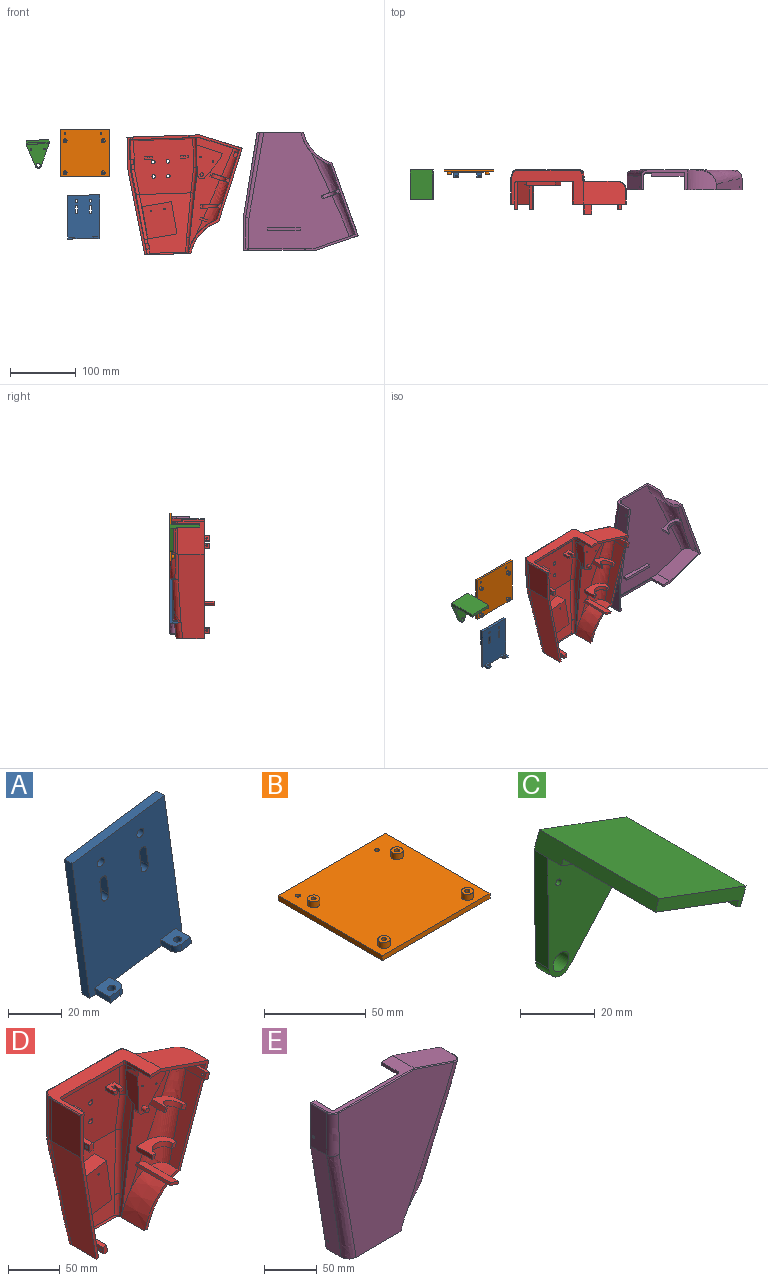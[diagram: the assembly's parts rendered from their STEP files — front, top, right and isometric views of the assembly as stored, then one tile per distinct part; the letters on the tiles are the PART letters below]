
ASSEMBLY  parts=5 mates=5
PART A: 28 faces, bbox 57.8x12x73 mm
  f0: plane 8x2.97mm, normal (-0.99,0,-0.14), area 24mm2, adj f1,f3,f4,f8
  f1: plane 8x7.92mm, normal (-0.14,0,0.99), area 55mm2, adj f0,f2,f4,f6,f7,f8
  f2: plane 5x2.97mm, normal (0.99,0,0.14), area 15mm2, adj f1,f3,f7,f8
  f3: plane 48.52x12mm, normal (0.14,0,-0.99), area 306mm2, adj f0,f2,f4,f5,f6,f7,f8,f9
  f4: plane 5.37x3.67mm, normal (0,-1,0), area 15mm2, adj f0,f1,f3,f7
  f5: plane 72.97x57.82mm, normal (0,1,0), area 3171mm2, adj f3,f15,f16,f17,f18,f19,f20,f21
  f6: cylinder r=1.5mm len=3.39mm, axis (0.14,0,-0.99), area 28.3mm2, adj f1,f3
  f7: cylinder r=3mm len=3.39mm, axis (-0.14,0,0.99), area 14.1mm2, adj f1,f2,f3,f4
  f8: plane 72.97x57.82mm, normal (0,-1,0), area 3123mm2, adj f0,f1,f2,f3,f9,f10,f11,f15
  f9: plane 5x2.97mm, normal (-0.99,0,-0.14), area 15mm2, adj f3,f8,f10,f14
  f10: plane 8x7.92mm, normal (-0.14,0,0.99), area 55mm2, adj f8,f9,f11,f12,f13,f14
  f11: plane 8x2.97mm, normal (0.99,0,0.14), area 24mm2, adj f3,f8,f10,f12
  f12: plane 5.37x3.67mm, normal (0,-1,0), area 15mm2, adj f3,f10,f11,f14
  f13: cylinder r=1.5mm len=3.39mm, axis (0.14,0,-0.99), area 28.3mm2, adj f3,f10
  f14: cylinder r=3mm len=3.39mm, axis (0.14,0,-0.99), area 14.1mm2, adj f3,f9,f10,f12
  f15: plane 48.52x6.82mm, normal (-0.14,0,0.99), area 196mm2, adj f5,f8,f16,f17
  f16: plane 66.15x9.3mm, normal (0.99,0,0.14), area 267.2mm2, adj f3,f5,f8,f15
  f17: plane 66.15x9.3mm, normal (-0.99,0,-0.14), area 267.2mm2, adj f3,f5,f8,f15
  f18: cylinder r=1.85mm len=4mm, axis (0,1,0), area 46.5mm2, adj f5,f8
  f19: cylinder r=1.85mm len=4mm, axis (0,1,0), area 46.5mm2, adj f5,f8
  f20: plane 7.92x4mm, normal (-0.99,0,-0.14), area 32mm2, adj f5,f8,f21,f23
  f21: cylinder r=1.85mm len=4mm, axis (0,-1,0), area 23.2mm2, adj f5,f8,f20,f22
  f22: plane 7.92x4mm, normal (0.99,0,0.14), area 32mm2, adj f5,f8,f21,f23
  f23: cylinder r=1.85mm len=4mm, axis (0,-1,0), area 23.2mm2, adj f5,f8,f20,f22
  f24: plane 7.92x4mm, normal (-0.99,0,-0.14), area 32mm2, adj f5,f8,f25,f27
  f25: cylinder r=1.85mm len=4mm, axis (0,-1,0), area 23.2mm2, adj f5,f8,f24,f26
  f26: plane 7.92x4mm, normal (0.99,0,0.14), area 32mm2, adj f5,f8,f25,f27
  f27: cylinder r=1.85mm len=4mm, axis (0,-1,0), area 23.2mm2, adj f5,f8,f24,f26
PART B: 20 faces, bbox 75x72.5x6.5 mm
  f0: plane 75x3mm, normal (0,-1,0), area 225mm2, adj f1,f3,f4,f5
  f1: plane 75x72.5mm, normal (0,0,-1), area 5408mm2, adj f0,f2,f3,f4,f14,f15,f16,f17
  f2: plane 75x3mm, normal (0,1,0), area 225mm2, adj f1,f3,f4,f5
  f3: plane 72.5x3mm, normal (1,0,0), area 217.5mm2, adj f0,f1,f2,f5
  f4: plane 72.5x3mm, normal (-1,0,0), area 217.5mm2, adj f0,f1,f2,f5
  f5: plane 75x72.5mm, normal (0,0,1), area 5314.6mm2, adj f0,f2,f3,f4,f6,f8,f10,f12
  f6: cylinder r=3mm len=6mm, axis (0,0,-1), area 66mm2, adj f5,f7
  f7: plane 6x6mm, normal (0,0,1), area 23.4mm2, adj f6,f14
  f8: cylinder r=3mm len=6mm, axis (0,0,-1), area 66mm2, adj f5,f9
  f9: plane 6x6mm, normal (0,0,1), area 23.4mm2, adj f8,f15
  f10: cylinder r=3mm len=6mm, axis (0,0,-1), area 66mm2, adj f5,f11
  f11: plane 6x6mm, normal (0,0,1), area 23.4mm2, adj f10,f17
  f12: cylinder r=3mm len=6mm, axis (0,0,-1), area 66mm2, adj f5,f13
  f13: plane 6x6mm, normal (0,0,1), area 23.4mm2, adj f12,f16
  f14: cylinder r=1.25mm len=6.5mm, axis (0,0,-1), area 51.1mm2, adj f1,f7
  f15: cylinder r=1.25mm len=6.5mm, axis (0,0,-1), area 51.1mm2, adj f1,f9
  f16: cylinder r=1.25mm len=6.5mm, axis (0,0,-1), area 51.1mm2, adj f1,f13
  f17: cylinder r=1.25mm len=6.5mm, axis (0,0,-1), area 51.1mm2, adj f1,f11
  f18: cylinder r=1.25mm len=3mm, axis (0,0,-1), area 23.6mm2, adj f1,f5
  f19: cylinder r=1.25mm len=3mm, axis (0,0,-1), area 23.6mm2, adj f1,f5
PART C: 16 faces, bbox 34.9x45.1x46.6 mm
  f0: plane 34.75x31.39mm, normal (-0.35,0,-0.94), area 1164.4mm2, adj f3,f4,f5,f6
  f1: plane 45.1x5.62mm, normal (0.94,0,-0.35), area 270.6mm2, adj f2,f4,f7,f8,f12
  f2: plane 45.1x32.79mm, normal (0.35,0,0.94), area 1578.5mm2, adj f1,f3,f4,f12
  f3: plane 45.1x5.62mm, normal (-0.94,0,0.35), area 201.1mm2, adj f0,f2,f4,f6,f7,f10,f12
  f4: plane 34.19x17.86mm, normal (0,-1,0), area 143mm2, adj f0,f1,f2,f3,f5,f7
  f5: plane 34.75x1.87mm, normal (-0.94,0,0.35), area 69.5mm2, adj f0,f4,f6,f7
  f6: plane 32.09x13.59mm, normal (0,-1,0), area 67mm2, adj f0,f3,f5,f7
  f7: plane 40x32.79mm, normal (-0.35,0,-0.94), area 235.6mm2, adj f1,f3,f4,f5,f6,f13
  f8: plane 27.21x24.34mm, normal (0.75,0,-0.67), area 186.2mm2, adj f1,f9,f12,f13
  f9: cylinder r=4.53mm len=7.9mm, axis (0,-1,0), area 55.3mm2, adj f8,f10,f12,f13
  f10: plane 36.5x5.1mm, normal (-1,0,-0.02), area 186.2mm2, adj f3,f9,f12,f13
  f11: cylinder r=3mm len=6mm, axis (0,-1,0), area 96.1mm2, adj f12,f13
  f12: plane 46.58x34.89mm, normal (0,1,0), area 931.4mm2, adj f1,f2,f3,f8,f9,f10,f11,f14
  f13: plane 40.96x32.79mm, normal (0,-1,0), area 721.4mm2, adj f7,f8,f9,f10,f11,f14,f15
  f14: cylinder r=1mm len=5.1mm, axis (0,-1,0), area 32mm2, adj f12,f13
  f15: cylinder r=1mm len=5.1mm, axis (0,-1,0), area 32mm2, adj f12,f13
PART D: 191 faces, bbox 178.3x70.2x193.3 mm
  f0: plane 89.97x78.42mm, normal (0,-0.99,0.11), area 3717.7mm2, adj f6,f22,f24,f26,f96,f97,f99,f100
  f1: bspline ~107.95x56.06mm, area 927.7mm2, adj f2,f93,f162,f176
  f2: plane 175.95x74.2mm, normal (0,-1,0), area 3207.5mm2, adj f1,f3,f4,f17,f21,f30,f76,f77
  f3: bspline ~141.8x71.41mm, area 740.7mm2, adj f2,f21,f93,f168,f169,f171,f174,f175
  f4: bspline ~118.22x59.84mm, area 747.7mm2, adj f2,f93,f94,f105,f107,f108,f109,f161
  f5: plane 14.86x7.7mm, normal (-0.99,-0.14,0), area 104.2mm2, adj f77,f82,f83,f95,f147
  f6: plane 90.13x82.27mm, normal (0,-1,0), area 6994.7mm2, adj f0,f83,f95,f96,f98,f99,f101,f102
  f7: plane 180x24.73mm, normal (0,-1,0), area 644.5mm2, adj f10,f20,f27,f32,f75,f91,f92,f124
  f8: plane 180x86.88mm, normal (0,-1,0), area 927.3mm2, adj f11,f21,f27,f30,f33,f34,f62,f93
  f9: plane 178.26x71.96mm, normal (0,1,0), area 4250mm2, adj f11,f14,f35,f42,f64,f125
  f10: plane 130x39.85mm, normal (-0.99,0,-0.16), area 4906.6mm2, adj f7,f16,f32,f45,f48,f125
  f11: cylinder r=64.67mm len=47mm, axis (0,-1,0), area 2206.9mm2, adj f8,f9,f33,f35,f125
  f12: plane 130x18.82mm, normal (0.99,0,-0.14), area 666.7mm2, adj f14,f15,f36,f44,f125
  f13: bspline ~98.25x68.46mm, area 5292.6mm2, adj f15,f16,f50,f53,f54,f58,f125
  f14: bspline ~148.6x23.11mm, area 156.7mm2, adj f9,f12,f42,f125
  f15: bspline ~46x11.51mm, area 150.9mm2, adj f12,f13,f51,f52,f125
  f16: bspline ~41.39x16.37mm, area 394mm2, adj f10,f13,f54,f125
  f17: plane 124.92x18.08mm, normal (-0.99,0,0.14), area 441.8mm2, adj f2,f22,f79,f125,f152
  f18: plane 130.24x21.22mm, normal (0.99,0,0.16), area 659.8mm2, adj f19,f26,f86,f87,f125
  f19: plane 175.58x21.36mm, normal (0,1,0), area 21.9mm2, adj f18,f20,f87,f88,f89,f92,f125
  f20: plane 130.33x30mm, normal (0.99,-0.02,0.16), area 3961.3mm2, adj f7,f19,f92,f125
  f21: cone r=68.17mm half-angle=1deg, axis (0,1,0), area 2093.4mm2, adj f2,f3,f8,f93,f125
  f22: bspline ~32.68x7.93mm, area 132.2mm2, adj f0,f17,f23,f97,f125
  f23: bspline ~3.21x3.08mm, area 1mm2, adj f22,f24,f125
  f24: cylinder r=5mm len=58.35mm, axis (1,0,0), area 133.2mm2, adj f0,f23,f25,f125
  f25: bspline ~3.17x3.08mm, area 1mm2, adj f24,f26,f125
  f26: bspline ~32.83x8.52mm, area 91.6mm2, adj f0,f18,f25,f100,f115,f117,f119,f125
  f27: plane 109x51mm, normal (0,0,1), area 2422.4mm2, adj f7,f8,f34,f66,f67,f68,f69,f70
  f28: plane 10.58x0.12mm, normal (0,1,0), area 1.3mm2, adj f29,f30,f76,f120
  f29: plane 100.2x5mm, normal (0,0,-1), area 78.9mm2, adj f28,f76,f78,f83,f89,f120,f121,f122
  f30: plane 31.53x14.45mm, normal (0,-0.02,-1), area 436.7mm2, adj f2,f8,f28,f76,f94,f120
  f31: plane 44.7x7.7mm, normal (0.99,-0.14,0), area 302.5mm2, adj f83,f84,f85,f86,f88,f98,f110,f112
  f32: plane 49.02x39.9mm, normal (-1,0,0), area 1954.2mm2, adj f7,f10,f48,f49,f75
  f33: plane 110.7x40.16mm, normal (0.94,0,-0.34), area 2131mm2, adj f8,f11,f35,f62
  f34: plane 64.09x35.05mm, normal (0.33,0,0.95), area 2273mm2, adj f8,f27,f62,f63,f64,f65,f66
  f35: bspline ~166.97x81.55mm, area 3387.4mm2, adj f9,f11,f33,f63
  f36: plane 49.01x5.25mm, normal (1,0,0), area 243.8mm2, adj f12,f42,f43,f44,f67
  f37: plane 96.53x95.72mm, normal (0,1,0), area 8197mm2, adj f55,f56,f58,f59,f60,f61,f71,f101
  f38: plane 48.85x5.69mm, normal (0.98,0.2,0), area 275.2mm2, adj f39,f43,f44,f55,f69
  f39: bspline ~140x24.17mm, area 1321.9mm2, adj f38,f44,f50,f51,f55,f56
  f40: bspline ~140x25mm, area 693.8mm2, adj f41,f45,f46,f48,f53,f60,f61
  f41: plane 48x4.9mm, normal (-0.93,0.37,0), area 246.5mm2, adj f40,f48,f49,f61,f73
  f42: bspline ~55.11x2mm, area 132.4mm2, adj f9,f14,f36,f65,f66
  f43: cylinder r=3mm len=48.99mm, axis (0,0,1), area 29mm2, adj f36,f38,f44,f68
  f44: bspline ~108.61x17.07mm, area 135.4mm2, adj f12,f36,f38,f39,f43,f51
  f45: bspline ~76.58x20.42mm, area 787.6mm2, adj f10,f40,f46,f47,f54
  f46: bspline ~5.02x4.67mm, area 3.1mm2, adj f40,f45,f47
  f47: bspline ~5.56x2.24mm, area 2.8mm2, adj f45,f46,f48
  f48: bspline ~41.83x8.47mm, area 180.9mm2, adj f10,f32,f40,f41,f47,f49
  f49: cylinder r=11mm len=48.97mm, axis (0,0,1), area 202.9mm2, adj f32,f41,f48,f74
  f50: bspline ~83.47x9.1mm, area 70.1mm2, adj f13,f39,f52,f57
  f51: bspline ~15.55x5.27mm, area 29.2mm2, adj f15,f39,f44,f52
  f52: bspline ~2.96x1.03mm, area 0.1mm2, adj f15,f50,f51
  f53: bspline ~52.77x5.79mm, area 61.8mm2, adj f13,f40,f54,f59
  f54: bspline ~20.38x12.71mm, area 173mm2, adj f13,f16,f45,f53
  f55: cylinder r=5mm len=46.01mm, axis (0,0,-1), area 314.9mm2, adj f37,f38,f39,f56,f70
  f56: bspline ~42.17x23.6mm, area 184.1mm2, adj f37,f39,f55,f57
  f57: sphere r=5mm, area 0mm2, adj f50,f56,f58
  f58: bspline ~61.72x10.88mm, area 37.4mm2, adj f13,f37,f57,f59
  f59: bspline ~0.51x0.4mm, area 0mm2, adj f37,f53,f58,f60
  f60: bspline ~42.52x23.03mm, area 161.7mm2, adj f37,f40,f59,f61
  f61: cylinder r=5mm len=45.57mm, axis (0,0,-1), area 270.4mm2, adj f37,f40,f41,f60,f72
  f62: cylinder r=1mm len=22mm, axis (0,-1,0), area 34.8mm2, adj f8,f33,f34,f63
  f63: bspline ~17x16.41mm, area 31.3mm2, adj f34,f35,f62,f64
  f64: cylinder r=1mm len=50.72mm, axis (0.95,0,-0.33), area 83.7mm2, adj f9,f34,f63,f65
  f65: bspline ~2.49x1.82mm, area 3mm2, adj f34,f42,f64,f66
  f66: bspline ~2.96x1.75mm, area 2.9mm2, adj f27,f34,f42,f65,f67
  f67: cylinder r=1mm len=4.71mm, axis (0,1,0), area 7.4mm2, adj f27,f36,f66,f68
  f68: torus R=2mm, axis (0,0,1), area 0.8mm2, adj f27,f43,f67,f69
  f69: cylinder r=1mm len=5.89mm, axis (-0.2,0.98,0), area 9.1mm2, adj f27,f38,f68,f70
  f70: torus R=4mm, axis (0,0,1), area 10mm2, adj f27,f55,f69,f71
  f71: cylinder r=1mm len=96.52mm, axis (1,0,0), area 151.6mm2, adj f27,f37,f70,f72
  f72: torus R=4mm, axis (0,0,1), area 8.7mm2, adj f27,f61,f71,f73
  f73: cylinder r=1mm len=5.26mm, axis (-0.37,-0.93,0), area 8.3mm2, adj f27,f41,f72,f74
  f74: torus R=10mm, axis (0,0,1), area 6.4mm2, adj f27,f49,f73,f75
  f75: cylinder r=1mm len=39.88mm, axis (0,-1,0), area 62.6mm2, adj f7,f27,f32,f74
  f76: cylinder r=1mm len=5mm, axis (0,-1,0), area 6.3mm2, adj f2,f28,f29,f30,f77,f82
  f77: plane 11.96x3.5mm, normal (-1,0,0), area 41.9mm2, adj f2,f5,f76,f147
  f78: plane 1.58x0.12mm, normal (0,1,0), area 0.2mm2, adj f29,f89,f91,f124
  f79: plane 106.37x14.61mm, normal (-0.98,-0.14,0.14), area 552.3mm2, adj f17,f80,f81,f96,f97,f152
  f80: cone r=1mm half-angle=8deg, axis (0,-1,0), area 0mm2, adj f79,f81,f152
  f81: plane 14.67x1.59mm, normal (-0.99,-0.14,0), area 11.8mm2, adj f79,f80,f95,f152
  f82: cone r=1mm half-angle=8deg, axis (0,-1,0), area 5.6mm2, adj f5,f76,f83
  f83: plane 100.46x12.26mm, normal (0,-0.14,-0.99), area 1203.1mm2, adj f5,f6,f29,f31,f82,f84,f95,f98
  f84: cone r=1mm half-angle=8deg, axis (0,-1,0), area 5.6mm2, adj f31,f83,f89
  f85: cone r=1mm half-angle=8deg, axis (0,-1,0), area 0.6mm2, adj f31,f86,f87
  f86: plane 106.5x17.33mm, normal (0.98,-0.14,0.16), area 571.3mm2, adj f18,f31,f85,f99,f100
  f87: cylinder r=1mm len=5mm, axis (0,-1,0), area 0.8mm2, adj f18,f19,f85,f88
  f88: plane 44.7x5mm, normal (1,0,0), area 223.5mm2, adj f19,f31,f87,f89
  f89: cylinder r=1mm len=5mm, axis (0,-1,0), area 7.1mm2, adj f19,f29,f78,f84,f88,f90,f91,f92
  f90: plane 0.32x0.32mm, normal (0,-1,0), area 0mm2, adj f89,f91,f92
  f91: plane 31.53x2.53mm, normal (0,-0.02,-1), area 67.7mm2, adj f7,f78,f89,f90,f92,f124
  f92: plane 46.25x31.53mm, normal (1,-0.02,0), area 1378.8mm2, adj f7,f19,f20,f89,f90,f91
  f93: plane 105.64x37.84mm, normal (-0.94,-0.02,0.34), area 1878.9mm2, adj f1,f3,f4,f8,f21,f94,f160,f161
  f94: plane 61.48x31.79mm, normal (-0.33,-0.02,-0.95), area 2009.2mm2, adj f2,f4,f8,f30,f93
  f95: cylinder r=5mm len=44.66mm, axis (0,0,-1), area 307.9mm2, adj f5,f6,f81,f83,f96,f147,f152
  f96: cylinder r=5mm len=39.63mm, axis (-0.14,0,-0.99), area 279.6mm2, adj f0,f6,f79,f95,f97
  f97: cylinder r=5mm len=68.29mm, axis (-0.13,-0.11,-0.99), area 487.5mm2, adj f0,f22,f79,f96
  f98: cylinder r=5mm len=44.62mm, axis (0,0,1), area 264.3mm2, adj f6,f31,f83,f99,f110,f113,f114
  f99: cylinder r=5mm len=39.85mm, axis (-0.16,0,0.99), area 281.2mm2, adj f0,f6,f86,f98,f100
  f100: cylinder r=5mm len=68.35mm, axis (-0.14,0.11,0.98), area 488mm2, adj f0,f26,f86,f99
  f101: cylinder r=2.75mm len=5.5mm, axis (0,-1,0), area 86.4mm2, adj f6,f37
  f102: cylinder r=2.75mm len=5.5mm, axis (0,-1,0), area 86.4mm2, adj f6,f37
  f103: cylinder r=2.75mm len=5.5mm, axis (0,-1,0), area 86.4mm2, adj f6,f37
  f104: cylinder r=2.75mm len=5.5mm, axis (0,-1,0), area 86.4mm2, adj f6,f37
  f105: plane 38.4x4.87mm, normal (-0.34,0,-0.94), area 179.8mm2, adj f4,f106,f107,f108
  f106: plane 9.22x7.4mm, normal (0,-1,0), area 40mm2, adj f105,f107,f108,f109
  f107: plane 38.57x7.55mm, normal (-0.94,0,0.34), area 302.3mm2, adj f4,f105,f106,f109,f128
  f108: plane 32.47x7.54mm, normal (0.94,0,-0.34), area 252.3mm2, adj f4,f105,f106,f109,f128
  f109: plane 38.69x4.85mm, normal (0.34,0,0.94), area 182.1mm2, adj f4,f106,f107,f108
  f110: plane 54.95x5mm, normal (0,0,-1), area 264.3mm2, adj f31,f98,f111,f112,f113
  f111: plane 8x5mm, normal (0,-1,0), area 40mm2, adj f110,f112,f113,f114
  f112: plane 45.13x8mm, normal (-1,0,0), area 356.2mm2, adj f31,f110,f111,f114,f126
  f113: plane 54.95x8mm, normal (1,0,0), area 434.7mm2, adj f98,f110,f111,f114,f126
  f114: plane 54.95x5mm, normal (0,0,1), area 264.3mm2, adj f31,f98,f111,f112,f113
  f115: plane 45.67x5.02mm, normal (0.16,0,-0.99), area 225.3mm2, adj f0,f26,f116,f117,f118
  f116: plane 8.7x6.22mm, normal (0,-1,0), area 40mm2, adj f115,f117,f118,f119
  f117: plane 43.99x8.17mm, normal (-0.99,0,-0.16), area 343.8mm2, adj f26,f115,f116,f119,f127
  f118: plane 46.48x7.9mm, normal (0.99,0,0.16), area 363.4mm2, adj f0,f115,f116,f119,f127
  f119: plane 46.63x5.08mm, normal (-0.16,0,0.99), area 228.9mm2, adj f0,f26,f116,f117,f118
  f120: plane 32.76x4.02mm, normal (-1,0,0), area 123.6mm2, adj f8,f27,f28,f29,f30,f121
  f121: cylinder r=2mm len=3.9mm, axis (0,0,1), area 12.3mm2, adj f27,f29,f120,f122
  f122: plane 85x3.9mm, normal (0,-1,0), area 331.5mm2, adj f27,f29,f121,f123
  f123: cylinder r=2mm len=3.9mm, axis (0,0,1), area 12.3mm2, adj f27,f29,f122,f124
  f124: plane 32.76x4.02mm, normal (1,0,0), area 123.6mm2, adj f7,f27,f29,f78,f91,f123
  f125: plane 71.33x43.65mm, normal (0,0,-1), area 713mm2, adj f2,f7,f8,f9,f10,f11,f12,f13
  f126: cylinder r=1.25mm len=5mm, axis (-1,0,0), area 39.3mm2, adj f112,f113
  f127: cylinder r=1.25mm len=5.34mm, axis (-0.99,0,-0.16), area 39.3mm2, adj f117,f118
  f128: cylinder r=1.25mm len=5.55mm, axis (0.94,0,-0.34), area 39.3mm2, adj f107,f108
  f129: plane 12x4mm, normal (1,0,0), area 48mm2, adj f6,f130,f136,f137
  f130: plane 4.25x4mm, normal (0,-1,0), area 17mm2, adj f129,f131,f136,f137
  f131: plane 8x4mm, normal (-1,0,0), area 32mm2, adj f130,f132,f136,f137
  f132: plane 4x3.5mm, normal (0,-1,0), area 14mm2, adj f131,f133,f136,f137
  f133: plane 8x4mm, normal (1,0,0), area 32mm2, adj f132,f134,f136,f137
  f134: plane 4.25x4mm, normal (0,-1,0), area 17mm2, adj f133,f135,f136,f137
  f135: plane 12x4mm, normal (-1,0,0), area 48mm2, adj f6,f134,f136,f137
  f136: plane 12x12mm, normal (0,0,-1), area 116mm2, adj f6,f129,f130,f131,f132,f133,f134,f135
  f137: plane 12x12mm, normal (0,0,1), area 116mm2, adj f6,f129,f130,f131,f132,f133,f134,f135
  f138: plane 12x4mm, normal (1,0,0), area 48mm2, adj f6,f139,f145,f146
  f139: plane 4.25x4mm, normal (0,-1,0), area 17mm2, adj f138,f140,f145,f146
  f140: plane 8x4mm, normal (-1,0,0), area 32mm2, adj f139,f141,f145,f146
  f141: plane 4x3.5mm, normal (0,-1,0), area 14mm2, adj f140,f142,f145,f146
  f142: plane 8x4mm, normal (1,0,0), area 32mm2, adj f141,f143,f145,f146
  f143: plane 4.25x4mm, normal (0,-1,0), area 17mm2, adj f142,f144,f145,f146
  f144: plane 12x4mm, normal (-1,0,0), area 48mm2, adj f6,f143,f145,f146
  f145: plane 12x12mm, normal (0,0,-1), area 116mm2, adj f6,f138,f139,f140,f141,f142,f143,f144
  f146: plane 12x12mm, normal (0,0,1), area 116mm2, adj f6,f138,f139,f140,f141,f142,f143,f144
  f147: plane 17.14x5mm, normal (-0.94,0,0.35), area 55.7mm2, adj f2,f5,f77,f95,f148,f150,f152
  f148: plane 37.7x14.07mm, normal (0.35,0,0.94), area 197.2mm2, adj f2,f147,f149,f150
  f149: plane 7.85x4.9mm, normal (0.94,0,-0.35), area 41mm2, adj f2,f148,f150,f151
  f150: plane 51.58x39.52mm, normal (0,-1,0), area 1222mm2, adj f147,f148,f149,f151,f152,f153,f154,f156
  f151: plane 27.49x24.59mm, normal (0.75,0,-0.67), area 180.7mm2, adj f2,f149,f150,f153
  f152: plane 40.28x17.03mm, normal (-1,0,-0.02), area 557.1mm2, adj f2,f17,f79,f80,f81,f95,f147,f150
  f153: cylinder r=6.53mm len=11.39mm, axis (0,-1,0), area 76.6mm2, adj f2,f150,f151,f152
  f154: cylinder r=2.65mm len=6mm, axis (0,1,0), area 99.9mm2, adj f150,f155
  f155: plane 5.3x5.3mm, normal (0,-1,0), area 22.1mm2, adj f154
  f156: cylinder r=1mm len=4.9mm, axis (0,-1,0), area 30.8mm2, adj f150,f159
  f157: cylinder r=1mm len=4.9mm, axis (0,-1,0), area 30.8mm2, adj f150,f158
  f158: plane 2x2mm, normal (0,-1,0), area 3.1mm2, adj f157
  f159: plane 2x2mm, normal (0,-1,0), area 3.1mm2, adj f156
  f160: plane 7.29x7.09mm, normal (0,-1,0), area 31.8mm2, adj f93,f161,f162,f165
  f161: plane 29.07x21.95mm, normal (0.34,0,0.94), area 402.9mm2, adj f2,f4,f93,f160,f163,f164,f165,f166
  f162: plane 29.08x21.97mm, normal (-0.34,0,-0.94), area 399.7mm2, adj f1,f2,f93,f160,f163,f164,f165,f166
  f163: plane 6.25x4.18mm, normal (0,-1,0), area 14mm2, adj f161,f162,f164,f166
  f164: plane 21.5x5.41mm, normal (-0.94,0,0.34), area 123.5mm2, adj f2,f161,f162,f163
  f165: plane 5.45x1.83mm, normal (-0.95,0,0.32), area 2.9mm2, adj f160,f161,f162,f167
  f166: plane 5.45x1.83mm, normal (0.95,0,-0.32), area 2.9mm2, adj f161,f162,f163,f167
  f167: cylinder r=11.2mm len=23.2mm, axis (0.32,0,0.95), area 202.1mm2, adj f161,f162,f165,f166
  f168: plane 45.22x3.01mm, normal (0.94,0,-0.34), area 144.4mm2, adj f3,f169,f171,f172
  f169: plane 46.72x11.52mm, normal (0.34,0,0.94), area 555.2mm2, adj f2,f3,f168,f170,f172
  f170: plane 46.5x3.01mm, normal (-0.94,0,0.34), area 148.6mm2, adj f2,f169,f171,f172
  f171: plane 46.7x11.51mm, normal (-0.34,0,-0.94), area 554.9mm2, adj f2,f3,f168,f170,f172
  f172: plane 12.38x7.04mm, normal (0,-1,0), area 38.4mm2, adj f168,f169,f170,f171
  f173: plane 6.97x5.52mm, normal (0,-1,0), area 27mm2, adj f93,f174,f175,f176,f179
  f174: plane 8.1x5.28mm, normal (0.91,0,-0.42), area 24.2mm2, adj f3,f93,f173,f175
  f175: plane 32.71x23.44mm, normal (0,0,-1), area 371.5mm2, adj f2,f3,f173,f174,f177,f178,f179,f180
  f176: plane 36.02x24.34mm, normal (0,0,1), area 420.7mm2, adj f1,f2,f93,f173,f177,f178,f179,f180
  f177: plane 5.52x4.44mm, normal (0,-1,0), area 19.4mm2, adj f175,f176,f178,f180
  f178: plane 21.5x5.52mm, normal (-1,0,0), area 118.6mm2, adj f2,f175,f176,f177
  f179: plane 5.52x1.85mm, normal (-0.95,0,0.32), area 2.9mm2, adj f173,f175,f176,f181
  f180: plane 5.52x1.85mm, normal (0.95,0,-0.32), area 2.9mm2, adj f175,f176,f177,f181
  f181: cylinder r=11.2mm len=25.48mm, axis (0.32,0,0.95), area 204.8mm2, adj f175,f176,f179,f180
  f182: plane 44.56x10.97mm, normal (0.14,0,-0.99), area 477.7mm2, adj f0,f183,f184,f185
  f183: plane 49.51x16.6mm, normal (0.99,0,0.14), area 689.2mm2, adj f0,f182,f184,f186
  f184: plane 55.78x51.52mm, normal (0,-1,0), area 2243.7mm2, adj f182,f183,f185,f186,f188,f190
  f185: plane 49.51x15.89mm, normal (-0.99,0,-0.14), area 653.6mm2, adj f0,f182,f184,f186
  f186: plane 44.56x16.6mm, normal (-0.14,0,0.99), area 730.8mm2, adj f0,f183,f184,f185
  f187: cone r=0mm half-angle=59deg, axis (0,-1,0), area 3.7mm2, adj f188
  f188: cylinder r=1mm len=5mm, axis (0,-1,0), area 31.4mm2, adj f184,f187
  f189: cone r=0mm half-angle=59deg, axis (0,-1,0), area 3.7mm2, adj f190
  f190: cylinder r=1mm len=5mm, axis (0,-1,0), area 31.4mm2, adj f184,f189
PART E: 49 faces, bbox 182.9x37x197 mm
  f0: plane 180x24.73mm, normal (0,1,0), area 644.5mm2, adj f2,f6,f10,f11,f12,f17,f23,f29
  f1: plane 180x86.88mm, normal (0,1,0), area 927.3mm2, adj f5,f9,f10,f11,f13,f14,f18,f24
  f2: plane 130x21.46mm, normal (-0.99,0,-0.16), area 2729.4mm2, adj f0,f4,f12,f33,f35
  f3: plane 179x155.19mm, normal (0,-1,0), area 19898.7mm2, adj f4,f5,f15,f16,f21,f22,f33
  f4: bspline ~136.37x31.87mm, area 1920.5mm2, adj f2,f3,f15,f33
  f5: cylinder r=64.67mm len=47mm, axis (0,-1,0), area 1869.5mm2, adj f1,f3,f13,f16,f33
  f6: plane 130.28x21.46mm, normal (0.99,0,0.16), area 2734.8mm2, adj f0,f8,f23,f33,f35
  f7: plane 176.5x153.48mm, normal (0,1,0), area 19128.4mm2, adj f8,f9,f10,f25,f26,f27,f33,f39
  f8: offset ~152.9x40.48mm, area 1195.3mm2, adj f6,f7,f26,f33
  f9: cylinder r=68.17mm len=49.8mm, axis (0,-1,0), area 1752.2mm2, adj f1,f7,f24,f27,f33
  f10: plane 106.06x26.65mm, normal (0,0,-1), area 602.4mm2, adj f0,f1,f7,f23,f25,f26,f28,f29
  f11: plane 109x29mm, normal (0,0,1), area 950.5mm2, adj f0,f1,f14,f17,f19,f21,f28,f29
  f12: plane 49x21.99mm, normal (-1,0,0), area 1059.7mm2, adj f0,f2,f15,f17,f34
  f13: plane 110.7x40.16mm, normal (0.94,0,-0.34), area 1544mm2, adj f1,f5,f16,f18,f36
  f14: plane 64.04x29mm, normal (0.33,0,0.95), area 1933.5mm2, adj f1,f11,f18,f20,f22
  f15: bspline ~50x8.54mm, area 631.5mm2, adj f3,f4,f12,f19
  f16: bspline ~166.97x81.55mm, area 3387.4mm2, adj f3,f5,f13,f20
  f17: cylinder r=1mm len=21.99mm, axis (0,1,0), area 34.5mm2, adj f0,f11,f12,f19
  f18: cylinder r=1mm len=17mm, axis (0,1,0), area 26.9mm2, adj f1,f13,f14,f20
  f19: bspline ~10.31x8.63mm, area 18.9mm2, adj f11,f15,f17,f21
  f20: bspline ~17x16.41mm, area 31.3mm2, adj f14,f16,f18,f22
  f21: cylinder r=1mm len=101.99mm, axis (1,0,0), area 160.1mm2, adj f3,f11,f19,f22
  f22: cylinder r=1mm len=53.02mm, axis (0.95,0,-0.33), area 87.4mm2, adj f3,f14,f20,f21
  f23: plane 46.22x21.96mm, normal (1,0,0), area 998.6mm2, adj f0,f6,f10,f26,f34
  f24: plane 105.66x37.7mm, normal (-0.94,0,0.34), area 1487.2mm2, adj f1,f9,f25,f27,f36
  f25: plane 61.43x26.83mm, normal (-0.33,0,-0.95), area 1693.2mm2, adj f1,f7,f10,f24,f27
  f26: offset ~53.22x15.54mm, area 345.5mm2, adj f7,f8,f10,f23
  f27: offset ~142.01x76.21mm, area 2454.2mm2, adj f7,f9,f24,f25,f38,f39,f41
  f28: plane 22.74x3.5mm, normal (-1,0,0), area 79.6mm2, adj f1,f10,f11,f32
  f29: plane 22.74x3.5mm, normal (1,0,0), area 79.6mm2, adj f0,f10,f11,f30
  f30: cylinder r=2mm len=3.5mm, axis (0,0,1), area 11mm2, adj f10,f11,f29,f31
  f31: plane 85x3.5mm, normal (0,1,0), area 297.5mm2, adj f10,f11,f30,f32
  f32: cylinder r=2mm len=3.5mm, axis (0,0,1), area 11mm2, adj f10,f11,f28,f31
  f33: plane 70.96x30.72mm, normal (0,0,-1), area 422.5mm2, adj f0,f1,f2,f3,f4,f5,f6,f7
  f34: cylinder r=1.25mm len=3.5mm, axis (-1,0,0), area 27.5mm2, adj f12,f23
  f35: cylinder r=1.25mm len=3.86mm, axis (-0.99,0,-0.16), area 27.5mm2, adj f2,f6
  f36: cylinder r=1.25mm len=4.14mm, axis (0.94,0,-0.34), area 27.5mm2, adj f13,f24
  f37: plane 6.73x6.54mm, normal (0,1,0), area 27.1mm2, adj f38,f39,f41,f43
  f38: plane 4.71x2.19mm, normal (0.94,0,-0.34), area 9.8mm2, adj f27,f37,f39,f41
  f39: plane 27.72x13.14mm, normal (-0.34,0,-0.94), area 200.4mm2, adj f7,f27,f37,f38,f40,f42,f43
  f40: plane 5.42x3.58mm, normal (0,1,0), area 10.3mm2, adj f39,f41,f42,f43
  f41: plane 27.71x13.12mm, normal (0.34,0,0.94), area 203.3mm2, adj f7,f27,f37,f38,f40,f42,f43
  f42: plane 12.5x4.71mm, normal (-0.94,0,0.34), area 62.5mm2, adj f7,f39,f40,f41
  f43: cylinder r=11.2mm len=21.89mm, axis (-0.32,0,-0.95), area 140.4mm2, adj f37,f39,f40,f41
  f44: plane 6x4mm, normal (1,0,0), area 24mm2, adj f7,f46,f47,f48
  f45: plane 6x4mm, normal (-1,0,0), area 24mm2, adj f7,f46,f47,f48
  f46: plane 50x6mm, normal (0,0,-1), area 300mm2, adj f7,f44,f45,f48
  f47: plane 50x6mm, normal (0,0,1), area 300mm2, adj f7,f44,f45,f48
  f48: plane 50x4mm, normal (0,1,0), area 200mm2, adj f44,f45,f46,f47
PLACE A rot(axis=(0,1,0),7.6deg) t=(-94.91,-56.04,-30.63)mm
PLACE B rot(axis=(1,0,0),90deg) t=(-112.77,42.33,44.62)mm
PLACE C rot(axis=(0,-1,0),22.3deg) t=(-220,-53.64,8.87)mm
PLACE D rot(axis=(0,-1,0),1.8deg) t=(16.83,-79.04,-16.28)mm
PLACE E rot(axis=(1,0,0),180deg) t=(190.76,-57.04,6.78)mm
MATE planar C.f12 <-> D.f37  axis (0,1,0) through (-256.93,-27.04,59.23)mm
MATE parallel D.f27 <-> C.f2  axis (-0.03,0,1) through (-59.53,-43.55,81.23)mm
MATE planar A.f5 <-> D.f37  axis (0,1,0) through (-187.18,-27.04,-42.66)mm
MATE planar E.f3 <-> D.f37  axis (0,1,0) through (129.88,-27.04,-14.66)mm
MATE planar B.f1 <-> D.f37  axis (0,1,0) through (-185.12,-27.04,55.34)mm
